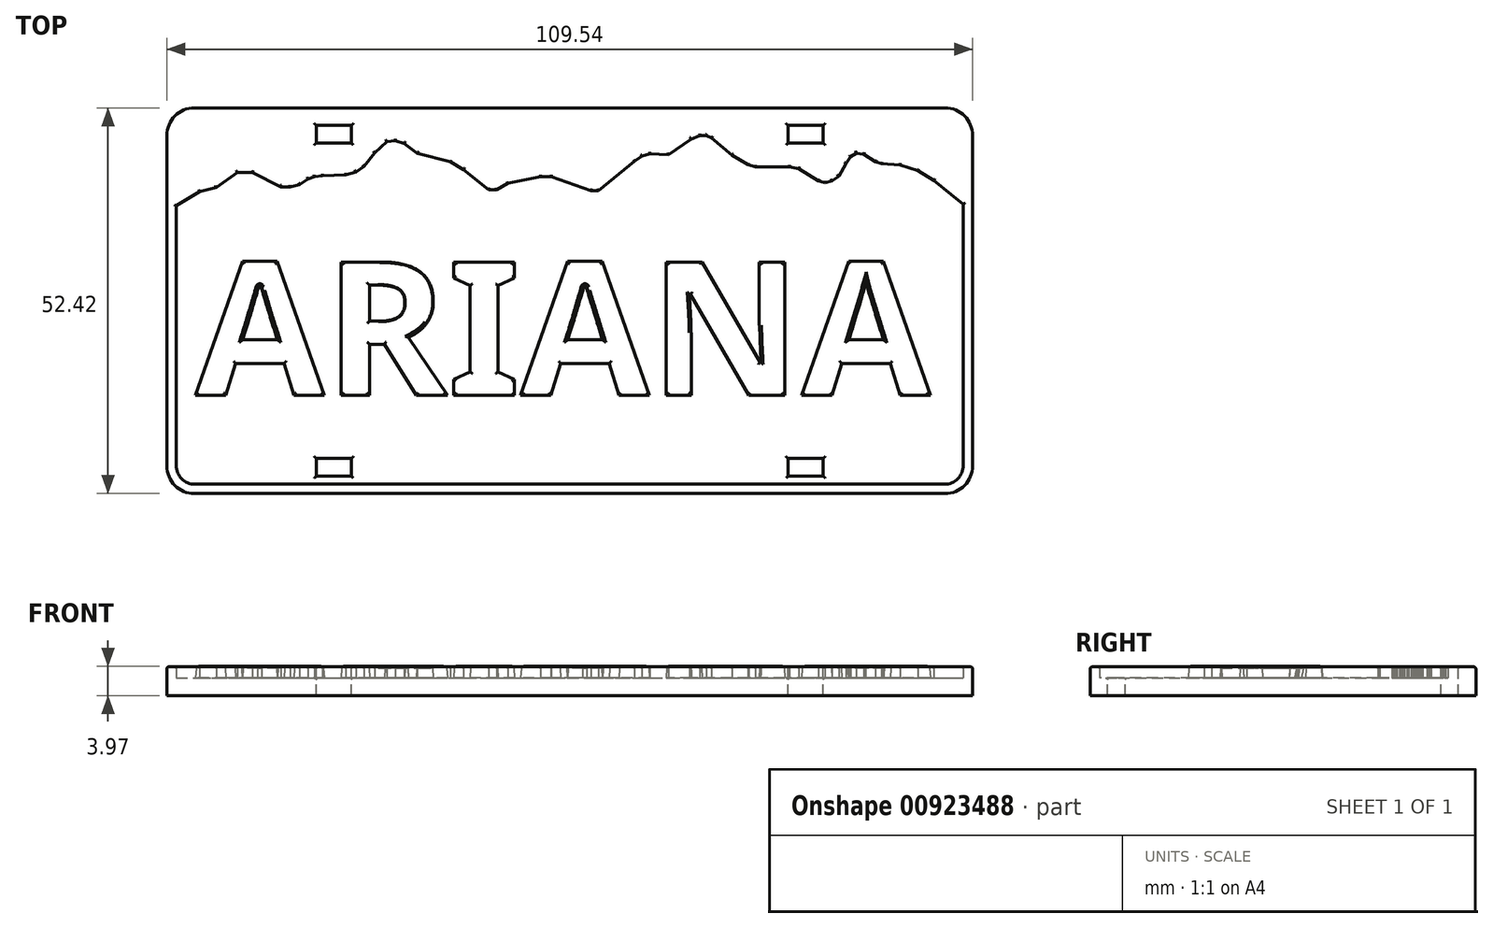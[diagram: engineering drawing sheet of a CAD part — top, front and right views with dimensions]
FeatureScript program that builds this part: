
annotation { "Feature Type Name" : "Feature", "Feature Type Description" : "" }
export const myFeature = defineFeature(function(context is Context, id is Id, definition is map)
    precondition{}
    {
        {
            var Q0;
            Q0=qCreatedBy(makeId("Top.planeOp"),FACE);
            var sketch = newSketch(context, id + "F0", { "sketchPlane" : qUnion([Q0])});
            skLineSegment(sketch, "E0", {"start": v(54.77, -22.46) * mm, "end": v(54.77, 22.46) * mm});
            skArc(sketch, "E1", {"start": v(54.77, 22.46) * mm, "mid": v(53.68, 25.11) * mm, "end": v(51.02, 26.21) * mm});
            skLineSegment(sketch, "E2", {"start": v(51.02, 26.21) * mm, "end": v(-51.02, 26.21) * mm});
            skArc(sketch, "E3", {"start": v(-51.02, 26.21) * mm, "mid": v(-53.68, 25.11) * mm, "end": v(-54.77, 22.46) * mm});
            skLineSegment(sketch, "E4", {"start": v(-54.77, 22.46) * mm, "end": v(-54.77, -22.46) * mm});
            skArc(sketch, "E5", {"start": v(-54.77, -22.46) * mm, "mid": v(-53.54, -25.24) * mm, "end": v(-50.64, -26.2) * mm});
            skLineSegment(sketch, "E6", {"start": v(-50.64, -26.2) * mm, "end": v(51.04, -26.2) * mm});
            skArc(sketch, "E7", {"start": v(51.02, -26.21) * mm, "mid": v(53.68, -25.11) * mm, "end": v(54.77, -22.46) * mm});
            skLineSegment(sketch, "E8", {"start": v(-54.77, 12.13) * mm, "end": v(-50.31, 14.84) * mm});
            skLineSegment(sketch, "E9", {"start": v(-50.31, 14.84) * mm, "end": v(-48.06, 15.4) * mm});
            skLineSegment(sketch, "E10", {"start": v(-48.06, 15.4) * mm, "end": v(-45.2, 17.44) * mm});
            skLineSegment(sketch, "E11", {"start": v(-45.2, 17.44) * mm, "end": v(-43.14, 17.44) * mm});
            skLineSegment(sketch, "E12", {"start": v(-43.14, 17.44) * mm, "end": v(-39.3, 15.5) * mm});
            skLineSegment(sketch, "E13", {"start": v(-39.3, 15.5) * mm, "end": v(-38.03, 15.49) * mm});
            skLineSegment(sketch, "E14", {"start": v(-38.03, 15.49) * mm, "end": v(-36.75, 15.8) * mm});
            skLineSegment(sketch, "E15", {"start": v(-36.75, 15.8) * mm, "end": v(-35.57, 16.54) * mm});
            skLineSegment(sketch, "E16", {"start": v(-35.57, 16.54) * mm, "end": v(-34.73, 16.88) * mm});
            skLineSegment(sketch, "E17", {"start": v(-34.73, 16.88) * mm, "end": v(-33.6, 17.01) * mm});
            skLineSegment(sketch, "E18", {"start": v(-33.6, 17.01) * mm, "end": v(-30.43, 17.11) * mm});
            skLineSegment(sketch, "E19", {"start": v(-29.05, 17.5) * mm, "end": v(-27.98, 18.27) * mm});
            skLineSegment(sketch, "E20", {"start": v(-27.98, 18.27) * mm, "end": v(-26.53, 20.14) * mm});
            skLineSegment(sketch, "E21", {"start": v(-26.53, 20.14) * mm, "end": v(-24.88, 21.63) * mm});
            skLineSegment(sketch, "E22", {"start": v(-24.88, 21.63) * mm, "end": v(-23.73, 21.77) * mm});
            skLineSegment(sketch, "E23", {"start": v(-22.5, 21.4) * mm, "end": v(-20.72, 20.04) * mm});
            skLineSegment(sketch, "E24", {"start": v(-16.23, 18.87) * mm, "end": v(-14.45, 17.85) * mm});
            skLineSegment(sketch, "E25", {"start": v(-14.45, 17.85) * mm, "end": v(-11.02, 15.1) * mm});
            skLineSegment(sketch, "E26", {"start": v(-11.02, 15.1) * mm, "end": v(-9.93, 15.1) * mm});
            skLineSegment(sketch, "E27", {"start": v(-9.93, 15.1) * mm, "end": v(-8.4, 15.96) * mm});
            skLineSegment(sketch, "E28", {"start": v(-8.4, 15.96) * mm, "end": v(-3.94, 16.85) * mm});
            skLineSegment(sketch, "E29", {"start": v(-3.94, 16.85) * mm, "end": v(-2.54, 16.85) * mm});
            skLineSegment(sketch, "E30", {"start": v(-2.54, 16.85) * mm, "end": v(2.9, 14.97) * mm});
            skLineSegment(sketch, "E31", {"start": v(2.9, 14.97) * mm, "end": v(3.92, 14.97) * mm});
            skLineSegment(sketch, "E32", {"start": v(3.92, 14.97) * mm, "end": v(8.8, 18.97) * mm});
            skLineSegment(sketch, "E33", {"start": v(8.8, 18.97) * mm, "end": v(9.82, 19.64) * mm});
            skLineSegment(sketch, "E34", {"start": v(9.82, 19.64) * mm, "end": v(10.9, 19.97) * mm});
            skLineSegment(sketch, "E35", {"start": v(10.9, 19.97) * mm, "end": v(13.43, 19.86) * mm});
            skLineSegment(sketch, "E36", {"start": v(16.5, 21.96) * mm, "end": v(17.71, 22.42) * mm});
            skLineSegment(sketch, "E37", {"start": v(17.71, 22.42) * mm, "end": v(18.56, 22.45) * mm});
            skLineSegment(sketch, "E38", {"start": v(18.56, 22.45) * mm, "end": v(19.28, 22.13) * mm});
            skLineSegment(sketch, "E39", {"start": v(19.28, 22.13) * mm, "end": v(22.05, 19.8) * mm});
            skLineSegment(sketch, "E40", {"start": v(22.05, 19.8) * mm, "end": v(24.2, 18.5) * mm});
            skLineSegment(sketch, "E41", {"start": v(24.2, 18.5) * mm, "end": v(25.23, 18.2) * mm});
            skLineSegment(sketch, "E42", {"start": v(25.23, 18.2) * mm, "end": v(29.85, 18.2) * mm});
            skLineSegment(sketch, "E43", {"start": v(29.85, 18.2) * mm, "end": v(31.13, 17.95) * mm});
            skLineSegment(sketch, "E44", {"start": v(31.13, 17.95) * mm, "end": v(33.84, 16.27) * mm});
            skLineSegment(sketch, "E45", {"start": v(33.84, 16.27) * mm, "end": v(34.73, 16.06) * mm});
            skLineSegment(sketch, "E46", {"start": v(34.73, 16.06) * mm, "end": v(35.67, 16.3) * mm});
            skLineSegment(sketch, "E47", {"start": v(35.67, 16.3) * mm, "end": v(36.58, 16.95) * mm});
            skLineSegment(sketch, "E48", {"start": v(36.58, 16.95) * mm, "end": v(37.58, 18.67) * mm});
            skLineSegment(sketch, "E49", {"start": v(38.22, 19.58) * mm, "end": v(38.96, 20.06) * mm});
            skLineSegment(sketch, "E50", {"start": v(38.96, 20.06) * mm, "end": v(39.94, 19.92) * mm});
            skLineSegment(sketch, "E51", {"start": v(41.58, 18.88) * mm, "end": v(42.4, 18.61) * mm});
            skLineSegment(sketch, "E52", {"start": v(42.4, 18.61) * mm, "end": v(44.9, 18.47) * mm});
            skLineSegment(sketch, "E53", {"start": v(44.9, 18.47) * mm, "end": v(47.31, 17.68) * mm});
            skLineSegment(sketch, "E54", {"start": v(47.31, 17.68) * mm, "end": v(49.47, 16.33) * mm});
            skLineSegment(sketch, "E55", {"start": v(49.47, 16.33) * mm, "end": v(51.88, 14.42) * mm});
            skLineSegment(sketch, "E56", {"start": v(51.88, 14.42) * mm, "end": v(53.78, 12.92) * mm});
            skLineSegment(sketch, "E57", {"start": v(53.78, 12.92) * mm, "end": v(54.77, 12.06) * mm});
            skLineSegment(sketch, "E58", {"start": v(-20.72, 20.04) * mm, "end": v(-16.23, 18.87) * mm});
            skLineSegment(sketch, "E59", {"start": v(16.5, 21.96) * mm, "end": v(13.43, 19.86) * mm});
            skLineSegment(sketch, "E60", {"start": v(-22.5, 21.4) * mm, "end": v(-23.73, 21.77) * mm});
            skLineSegment(sketch, "E61", {"start": v(-29.05, 17.5) * mm, "end": v(-30.43, 17.11) * mm});
            skLineSegment(sketch, "E62", {"start": v(37.58, 18.67) * mm, "end": v(38.22, 19.58) * mm});
            skLineSegment(sketch, "E63", {"start": v(41.58, 18.88) * mm, "end": v(39.94, 19.92) * mm});
            skSolve(sketch);
        }
        {
            var Q0;
            Q0=qCreatedBy(makeId("Top.planeOp"),FACE);
            var sketch = newSketch(context, id + "F1", { "sketchPlane" : qUnion([Q0])});
            skLineSegment(sketch, "E64", {"start": v(54.77, -22.46) * mm, "end": v(54.77, 22.46) * mm});
            skArc(sketch, "E65", {"start": v(54.77, 22.46) * mm, "mid": v(53.68, 25.11) * mm, "end": v(51.02, 26.21) * mm});
            skLineSegment(sketch, "E66", {"start": v(51.02, 26.21) * mm, "end": v(-51.02, 26.21) * mm});
            skArc(sketch, "E67", {"start": v(-51.02, 26.21) * mm, "mid": v(-53.68, 25.11) * mm, "end": v(-54.77, 22.46) * mm});
            skLineSegment(sketch, "E68", {"start": v(-54.77, 22.46) * mm, "end": v(-54.77, -22.46) * mm});
            skArc(sketch, "E69", {"start": v(-54.77, -22.46) * mm, "mid": v(-53.68, -25.11) * mm, "end": v(-51.02, -26.21) * mm});
            skLineSegment(sketch, "E70", {"start": v(-51.02, -26.21) * mm, "end": v(51.02, -26.21) * mm});
            skArc(sketch, "E71", {"start": v(51.02, -26.21) * mm, "mid": v(53.68, -25.11) * mm, "end": v(54.77, -22.46) * mm});
            skLineSegment(sketch, "E72.0", {"start": v(50.96, 24.94) * mm, "end": v(-50.96, 24.94) * mm, "construction": true});
            skLineSegment(sketch, "E72.1", {"start": v(53.5, -22.4) * mm, "end": v(53.5, 22.4) * mm, "construction": true});
            skLineSegment(sketch, "E72.2", {"start": v(-50.96, -24.94) * mm, "end": v(50.96, -24.94) * mm, "construction": true});
            skLineSegment(sketch, "E72.3", {"start": v(-53.5, 22.4) * mm, "end": v(-53.5, -22.4) * mm, "construction": true});
            skPoint(sketch, "E73.visualSharp", {"position": v(-53.5, 24.94) * mm});
            skArc(sketch, "E73.filletArc", {"start": v(-50.96, 24.94) * mm, "mid": v(-52.76, 24.2) * mm, "end": v(-53.5, 22.4) * mm, "construction": true});
            skPoint(sketch, "E74.visualSharp", {"position": v(-53.5, -24.94) * mm});
            skArc(sketch, "E74.filletArc", {"start": v(-53.5, -22.4) * mm, "mid": v(-52.76, -24.2) * mm, "end": v(-50.96, -24.94) * mm, "construction": true});
            skPoint(sketch, "E75.visualSharp", {"position": v(53.5, -24.94) * mm});
            skArc(sketch, "E75.filletArc", {"start": v(50.96, -24.94) * mm, "mid": v(52.76, -24.2) * mm, "end": v(53.5, -22.4) * mm, "construction": true});
            skPoint(sketch, "E76.visualSharp", {"position": v(53.5, 24.94) * mm});
            skArc(sketch, "E76.filletArc", {"start": v(53.5, 22.4) * mm, "mid": v(52.76, 24.2) * mm, "end": v(50.96, 24.94) * mm, "construction": true});
            skSolve(sketch);
        }
        {
            var Q0;
            {var subQ3=sQuery(id+"F0.wireOp",EDGE,"E1");Q0=makeQuery(id+"F0.imprint","IMPRINT",FACE,{"disambiguationData":[TD([[makeQuery(id+"F0.imprint","IMPRINT",EDGE,{"derivedFrom":subQ3}),1.0]])]});}
            extrude(context, id + "F2", {"entities" : qUnion([Q0]), "depth" : 1.52 * mm, "offsetDistance" : 25.4 * mm});
        }
        {
            var Q0;
            Q0=qSketchRegion(id+"F1",true);
            extrude(context, id + "F3", {"entities" : qUnion([Q0]), "operationType" : NewBodyOperationType.ADD, "oppositeDirection" : true, "depth" : 2.38 * mm, "offsetDistance" : 25.4 * mm});
        }
        {
            var Q0;
            {var subQ58=sQuery(id+"F0.wireOp",EDGE,"E0");var subQ59=sQuery(id+"F1.wireOp",EDGE,"E64");var subQ60=sQuery(id+"F1.wireOp",EDGE,"E65");var subQ61=sQuery(id+"F1.wireOp",EDGE,"E68");var subQ62=sQuery(id+"F1.wireOp",EDGE,"E69");var subQ63=sQuery(id+"F1.wireOp",EDGE,"E70");var subQ64=sQuery(id+"F1.wireOp",EDGE,"E71");Q0=makeQuery(id+"F3.boolean.opBoolean","SPLIT",FACE,{"disambiguationData":[TD([makeQuery(id+"F2.opExtrude","SWEPT_FACE",FACE,{"disambiguationData":[OSD([subQ58])]})])],"derivedFrom":makeQuery(id+"F3.opExtrude","CAP_FACE",FACE,{"disambiguationData":[OSD([subQ59,subQ60,sQuery(id+"F1.wireOp",EDGE,"E66"),sQuery(id+"F1.wireOp",EDGE,"E67"),subQ61,subQ62,subQ63,subQ64])],"isStart":true})});}
            var sketch = newSketch(context, id + "F4", { "sketchPlane" : qUnion([Q0])});
            skLineSegment(sketch, "E77", {"start": v(54.77, -22.46) * mm, "end": v(54.77, 12.06) * mm});
            skLineSegment(sketch, "E78", {"start": v(-54.77, 12.13) * mm, "end": v(-54.77, -22.46) * mm});
            skArc(sketch, "E79", {"start": v(-54.77, -22.46) * mm, "mid": v(-53.68, -25.11) * mm, "end": v(-51.02, -26.21) * mm});
            skLineSegment(sketch, "E80", {"start": v(-51.02, -26.21) * mm, "end": v(51.02, -26.21) * mm});
            skArc(sketch, "E81", {"start": v(51.02, -26.21) * mm, "mid": v(53.68, -25.11) * mm, "end": v(54.77, -22.46) * mm});
            skLineSegment(sketch, "E82.1", {"start": v(53.5, -22.4) * mm, "end": v(53.5, 13.14) * mm});
            skLineSegment(sketch, "E82.2", {"start": v(-50.96, -24.94) * mm, "end": v(50.96, -24.94) * mm});
            skLineSegment(sketch, "E82.3", {"start": v(-53.5, 12.9) * mm, "end": v(-53.5, -22.4) * mm});
            skPoint(sketch, "E83.visualSharp", {"position": v(-53.5, 24.94) * mm});
            skPoint(sketch, "E84.visualSharp", {"position": v(-53.5, -24.94) * mm});
            skArc(sketch, "E84.filletArc", {"start": v(-53.5, -22.4) * mm, "mid": v(-52.76, -24.2) * mm, "end": v(-50.96, -24.94) * mm});
            skPoint(sketch, "E85.visualSharp", {"position": v(53.5, -24.94) * mm});
            skArc(sketch, "E85.filletArc", {"start": v(50.96, -24.94) * mm, "mid": v(52.76, -24.2) * mm, "end": v(53.5, -22.4) * mm});
            skPoint(sketch, "E86.visualSharp", {"position": v(53.5, 24.94) * mm});
            skLineSegment(sketch, "E87", {"start": v(-54.77, 12.13) * mm, "end": v(-53.5, 12.9) * mm});
            skLineSegment(sketch, "E88", {"start": v(53.5, 13.14) * mm, "end": v(53.78, 12.92) * mm});
            skLineSegment(sketch, "E89", {"start": v(53.78, 12.92) * mm, "end": v(54.77, 12.06) * mm});
            skSolve(sketch);
        }
        {
            var Q0;
            Q0=qSketchRegion(id+"F4",true);
            extrude(context, id + "F5", {"entities" : qUnion([Q0]), "operationType" : NewBodyOperationType.ADD, "depth" : 1.52 * mm, "offsetDistance" : 25.4 * mm});
        }
        {
            var Q0;
            Q0=makeQuery(id+"F5.boolean.opBoolean","MERGE",FACE,{"derivedFrom":[makeQuery(id+"F2.opExtrude","CAP_FACE",FACE,{"disambiguationData":[OSD([sQuery(id+"F0.wireOp",EDGE,"E0"),sQuery(id+"F0.wireOp",EDGE,"E1"),sQuery(id+"F0.wireOp",EDGE,"E2"),sQuery(id+"F0.wireOp",EDGE,"E3"),sQuery(id+"F0.wireOp",EDGE,"E4"),sQuery(id+"F0.wireOp",EDGE,"E8"),sQuery(id+"F0.wireOp",EDGE,"E9"),sQuery(id+"F0.wireOp",EDGE,"E10"),sQuery(id+"F0.wireOp",EDGE,"E11"),sQuery(id+"F0.wireOp",EDGE,"E12"),sQuery(id+"F0.wireOp",EDGE,"E13"),sQuery(id+"F0.wireOp",EDGE,"E14"),sQuery(id+"F0.wireOp",EDGE,"E15"),sQuery(id+"F0.wireOp",EDGE,"E16"),sQuery(id+"F0.wireOp",EDGE,"E17"),sQuery(id+"F0.wireOp",EDGE,"E18"),sQuery(id+"F0.wireOp",EDGE,"7b9f405e-0691-426e-9c9e-a5372cf0836a"),sQuery(id+"F0.wireOp",EDGE,"E19"),sQuery(id+"F0.wireOp",EDGE,"E20"),sQuery(id+"F0.wireOp",EDGE,"E21"),sQuery(id+"F0.wireOp",EDGE,"E22"),sQuery(id+"F0.wireOp",EDGE,"b3dec5b1-662c-4d50-a13c-af7b7760114a"),sQuery(id+"F0.wireOp",EDGE,"E23"),sQuery(id+"F0.wireOp",EDGE,"4d9ee76e-0833-4cdc-b1a8-2d4ce76e6521"),sQuery(id+"F0.wireOp",EDGE,"E24"),sQuery(id+"F0.wireOp",EDGE,"E25"),sQuery(id+"F0.wireOp",EDGE,"E26"),sQuery(id+"F0.wireOp",EDGE,"E27"),sQuery(id+"F0.wireOp",EDGE,"E28"),sQuery(id+"F0.wireOp",EDGE,"E29"),sQuery(id+"F0.wireOp",EDGE,"E30"),sQuery(id+"F0.wireOp",EDGE,"E31"),sQuery(id+"F0.wireOp",EDGE,"E32"),sQuery(id+"F0.wireOp",EDGE,"E33"),sQuery(id+"F0.wireOp",EDGE,"E34"),sQuery(id+"F0.wireOp",EDGE,"E35"),sQuery(id+"F0.wireOp",EDGE,"55551997-bb9e-4b94-90c5-def3cb147476"),sQuery(id+"F0.wireOp",EDGE,"E36"),sQuery(id+"F0.wireOp",EDGE,"E37"),sQuery(id+"F0.wireOp",EDGE,"E38"),sQuery(id+"F0.wireOp",EDGE,"E39"),sQuery(id+"F0.wireOp",EDGE,"E40"),sQuery(id+"F0.wireOp",EDGE,"E41"),sQuery(id+"F0.wireOp",EDGE,"E42"),sQuery(id+"F0.wireOp",EDGE,"E43"),sQuery(id+"F0.wireOp",EDGE,"E44"),sQuery(id+"F0.wireOp",EDGE,"E45"),sQuery(id+"F0.wireOp",EDGE,"E46"),sQuery(id+"F0.wireOp",EDGE,"E47"),sQuery(id+"F0.wireOp",EDGE,"E48"),sQuery(id+"F0.wireOp",EDGE,"513b7cbe-d979-4e22-b277-f3c42ccdbda1"),sQuery(id+"F0.wireOp",EDGE,"E49"),sQuery(id+"F0.wireOp",EDGE,"E50"),sQuery(id+"F0.wireOp",EDGE,"0d842e13-672c-40e3-aae4-28923e78d4e0"),sQuery(id+"F0.wireOp",EDGE,"E51"),sQuery(id+"F0.wireOp",EDGE,"E52"),sQuery(id+"F0.wireOp",EDGE,"E53"),sQuery(id+"F0.wireOp",EDGE,"E54"),sQuery(id+"F0.wireOp",EDGE,"E55"),sQuery(id+"F0.wireOp",EDGE,"E56"),sQuery(id+"F0.wireOp",EDGE,"E57")])],"isStart":false}),makeQuery(id+"F5.opExtrude","CAP_FACE",FACE,{"disambiguationData":[OSD([sQuery(id+"F4.wireOp",EDGE,"E77"),sQuery(id+"F4.wireOp",EDGE,"E78"),sQuery(id+"F4.wireOp",EDGE,"E79"),sQuery(id+"F4.wireOp",EDGE,"E80"),sQuery(id+"F4.wireOp",EDGE,"E81"),sQuery(id+"F4.wireOp",EDGE,"E82.1"),sQuery(id+"F4.wireOp",EDGE,"E82.2"),sQuery(id+"F4.wireOp",EDGE,"E82.3"),sQuery(id+"F4.wireOp",EDGE,"E84.filletArc"),sQuery(id+"F4.wireOp",EDGE,"E85.filletArc"),sQuery(id+"F4.wireOp",EDGE,"E87"),sQuery(id+"F4.wireOp",EDGE,"E88"),sQuery(id+"F4.wireOp",EDGE,"E89")])],"isStart":false})]});
            var sketch = newSketch(context, id + "F6", { "sketchPlane" : qUnion([Q0])});
            skLineSegment(sketch, "E90.bottom", {"start": v(-34.45, 23.83) * mm, "end": v(-29.7, 23.83) * mm});
            skLineSegment(sketch, "E90.top", {"start": v(-34.45, 21.45) * mm, "end": v(-29.7, 21.45) * mm});
            skLineSegment(sketch, "E90.left", {"start": v(-34.45, 23.83) * mm, "end": v(-34.45, 21.45) * mm});
            skLineSegment(sketch, "E90.right", {"start": v(-29.7, 23.83) * mm, "end": v(-29.7, 21.45) * mm});
            skLineSegment(sketch, "E91", {"start": v(0, 26.21) * mm, "end": v(0, -26.21) * mm, "construction": true});
            skLineSegment(sketch, "E92.MirrorCS", {"start": v(34.45, 23.83) * mm, "end": v(34.45, 21.45) * mm});
            skLineSegment(sketch, "E93.MirrorCS", {"start": v(29.7, 23.83) * mm, "end": v(29.7, 21.45) * mm});
            skLineSegment(sketch, "E94.MirrorCS", {"start": v(34.45, 21.45) * mm, "end": v(29.7, 21.45) * mm});
            skLineSegment(sketch, "E95.MirrorCS", {"start": v(34.45, 23.83) * mm, "end": v(29.7, 23.83) * mm});
            skLineSegment(sketch, "E96", {"start": v(0, 0) * mm, "end": v(-59.23, 0) * mm, "construction": true});
            skLineSegment(sketch, "E97", {"start": v(0, 0) * mm, "end": v(56.47, 0) * mm, "construction": true});
            skLineSegment(sketch, "E98.MirrorCS", {"start": v(-34.45, -23.83) * mm, "end": v(-29.7, -23.83) * mm});
            skLineSegment(sketch, "E99.MirrorCS", {"start": v(-34.45, -23.83) * mm, "end": v(-34.45, -21.45) * mm});
            skLineSegment(sketch, "E100.MirrorCS", {"start": v(-34.45, -21.45) * mm, "end": v(-29.7, -21.45) * mm});
            skLineSegment(sketch, "E101.MirrorCS", {"start": v(-29.7, -23.83) * mm, "end": v(-29.7, -21.45) * mm});
            skLineSegment(sketch, "E102.MirrorCS", {"start": v(29.7, -23.83) * mm, "end": v(29.7, -21.45) * mm});
            skLineSegment(sketch, "E103.MirrorCS", {"start": v(34.45, -23.83) * mm, "end": v(29.7, -23.83) * mm});
            skLineSegment(sketch, "E104.MirrorCS", {"start": v(34.45, -23.83) * mm, "end": v(34.45, -21.45) * mm});
            skLineSegment(sketch, "E105.MirrorCS", {"start": v(34.45, -21.45) * mm, "end": v(29.7, -21.45) * mm});
            skSolve(sketch);
        }
        {
            var Q0;
            Q0=qSketchRegion(id+"F6",true);
            extrude(context, id + "F7", {"entities" : qUnion([Q0]), "operationType" : NewBodyOperationType.REMOVE, "endBound" : BoundingType.THROUGH_ALL, "oppositeDirection" : true, "depth" : 25.4 * mm, "offsetDistance" : 25.4 * mm});
        }
        {
            var Q0;
            Q0=makeQuery(id+"F3.opExtrude","CAP_FACE",FACE,{"disambiguationData":[OSD([sQuery(id+"F1.wireOp",EDGE,"E64"),sQuery(id+"F1.wireOp",EDGE,"E65"),sQuery(id+"F1.wireOp",EDGE,"E66"),sQuery(id+"F1.wireOp",EDGE,"E67"),sQuery(id+"F1.wireOp",EDGE,"E68"),sQuery(id+"F1.wireOp",EDGE,"E69"),sQuery(id+"F1.wireOp",EDGE,"E70"),sQuery(id+"F1.wireOp",EDGE,"E71")])],"isStart":true});
            var sketch = newSketch(context, id + "F8", { "sketchPlane" : qUnion([Q0])});
            skText(sketch, "E106", { "text": "ARIANA", "fontName": "NotoSans-Bold.ttf"});
            const initialGuessF8  = {"E106": [-0.0509, -0.01287, 1, 0, 0.0183]};
            skSetInitialGuess(sketch, initialGuessF8);
            skSolve(sketch);
        }
        {
            var Q0;
            Q0=qSketchRegion(id+"F8",true);
            extrude(context, id + "F9", {"entities" : qUnion([Q0]), "operationType" : NewBodyOperationType.ADD, "depth" : 1.59 * mm, "offsetDistance" : 25.4 * mm, "hasDraft" : true, "draftAngle" : 3 * degree, "draftPullDirection" : true});
        }
        {
            var Q0;
            Q0=makeQuery(id+"F5.boolean.opBoolean","MERGE",FACE,{"derivedFrom":[makeQuery(id+"F2.opExtrude","CAP_FACE",FACE,{"disambiguationData":[OSD([sQuery(id+"F0.wireOp",EDGE,"E0"),sQuery(id+"F0.wireOp",EDGE,"E1"),sQuery(id+"F0.wireOp",EDGE,"E2"),sQuery(id+"F0.wireOp",EDGE,"E3"),sQuery(id+"F0.wireOp",EDGE,"E4"),sQuery(id+"F0.wireOp",EDGE,"E8"),sQuery(id+"F0.wireOp",EDGE,"E9"),sQuery(id+"F0.wireOp",EDGE,"E10"),sQuery(id+"F0.wireOp",EDGE,"E11"),sQuery(id+"F0.wireOp",EDGE,"E12"),sQuery(id+"F0.wireOp",EDGE,"E13"),sQuery(id+"F0.wireOp",EDGE,"E14"),sQuery(id+"F0.wireOp",EDGE,"E15"),sQuery(id+"F0.wireOp",EDGE,"E16"),sQuery(id+"F0.wireOp",EDGE,"E17"),sQuery(id+"F0.wireOp",EDGE,"E18"),sQuery(id+"F0.wireOp",EDGE,"E19"),sQuery(id+"F0.wireOp",EDGE,"E20"),sQuery(id+"F0.wireOp",EDGE,"E21"),sQuery(id+"F0.wireOp",EDGE,"E22"),sQuery(id+"F0.wireOp",EDGE,"E23"),sQuery(id+"F0.wireOp",EDGE,"E24"),sQuery(id+"F0.wireOp",EDGE,"E25"),sQuery(id+"F0.wireOp",EDGE,"E26"),sQuery(id+"F0.wireOp",EDGE,"E27"),sQuery(id+"F0.wireOp",EDGE,"E28"),sQuery(id+"F0.wireOp",EDGE,"E29"),sQuery(id+"F0.wireOp",EDGE,"E30"),sQuery(id+"F0.wireOp",EDGE,"E31"),sQuery(id+"F0.wireOp",EDGE,"E32"),sQuery(id+"F0.wireOp",EDGE,"E33"),sQuery(id+"F0.wireOp",EDGE,"E34"),sQuery(id+"F0.wireOp",EDGE,"E35"),sQuery(id+"F0.wireOp",EDGE,"E36"),sQuery(id+"F0.wireOp",EDGE,"E37"),sQuery(id+"F0.wireOp",EDGE,"E38"),sQuery(id+"F0.wireOp",EDGE,"E39"),sQuery(id+"F0.wireOp",EDGE,"E40"),sQuery(id+"F0.wireOp",EDGE,"E41"),sQuery(id+"F0.wireOp",EDGE,"E42"),sQuery(id+"F0.wireOp",EDGE,"E43"),sQuery(id+"F0.wireOp",EDGE,"E44"),sQuery(id+"F0.wireOp",EDGE,"E45"),sQuery(id+"F0.wireOp",EDGE,"E46"),sQuery(id+"F0.wireOp",EDGE,"E47"),sQuery(id+"F0.wireOp",EDGE,"E48"),sQuery(id+"F0.wireOp",EDGE,"E49"),sQuery(id+"F0.wireOp",EDGE,"E50"),sQuery(id+"F0.wireOp",EDGE,"E51"),sQuery(id+"F0.wireOp",EDGE,"E52"),sQuery(id+"F0.wireOp",EDGE,"E53"),sQuery(id+"F0.wireOp",EDGE,"E54"),sQuery(id+"F0.wireOp",EDGE,"E55"),sQuery(id+"F0.wireOp",EDGE,"E56"),sQuery(id+"F0.wireOp",EDGE,"E57"),sQuery(id+"F0.wireOp",EDGE,"E58"),sQuery(id+"F0.wireOp",EDGE,"E59"),sQuery(id+"F0.wireOp",EDGE,"E60"),sQuery(id+"F0.wireOp",EDGE,"E61"),sQuery(id+"F0.wireOp",EDGE,"E62"),sQuery(id+"F0.wireOp",EDGE,"E63")])],"isStart":false}),makeQuery(id+"F5.opExtrude","CAP_FACE",FACE,{"disambiguationData":[OSD([sQuery(id+"F4.wireOp",EDGE,"E77"),sQuery(id+"F4.wireOp",EDGE,"E78"),sQuery(id+"F4.wireOp",EDGE,"E79"),sQuery(id+"F4.wireOp",EDGE,"E80"),sQuery(id+"F4.wireOp",EDGE,"E81"),sQuery(id+"F4.wireOp",EDGE,"E82.1"),sQuery(id+"F4.wireOp",EDGE,"E82.2"),sQuery(id+"F4.wireOp",EDGE,"E82.3"),sQuery(id+"F4.wireOp",EDGE,"E84.filletArc"),sQuery(id+"F4.wireOp",EDGE,"E85.filletArc"),sQuery(id+"F4.wireOp",EDGE,"E87"),sQuery(id+"F4.wireOp",EDGE,"E88"),sQuery(id+"F4.wireOp",EDGE,"E89")])],"isStart":false})]});
            var Q1;
            Q1=makeQuery(id+"F9.opExtrude","CAP_FACE",FACE,{"disambiguationData":[OSD([sQuery(id+"F8.wireOp",EDGE,"E106.sketch_text.stroke-0"),sQuery(id+"F8.wireOp",EDGE,"E106.sketch_text.stroke-1"),sQuery(id+"F8.wireOp",EDGE,"E106.sketch_text.stroke-2"),sQuery(id+"F8.wireOp",EDGE,"E106.sketch_text.stroke-3"),sQuery(id+"F8.wireOp",EDGE,"E106.sketch_text.stroke-4"),sQuery(id+"F8.wireOp",EDGE,"E106.sketch_text.stroke-5"),sQuery(id+"F8.wireOp",EDGE,"E106.sketch_text.stroke-6"),sQuery(id+"F8.wireOp",EDGE,"E106.sketch_text.stroke-7"),sQuery(id+"F8.wireOp",EDGE,"E106.sketch_text.stroke-8"),sQuery(id+"F8.wireOp",EDGE,"E106.sketch_text.stroke-9"),sQuery(id+"F8.wireOp",EDGE,"E106.sketch_text.stroke-10"),sQuery(id+"F8.wireOp",EDGE,"E106.sketch_text.stroke-11")])],"isStart":false});
            var Q2;
            Q2=makeQuery(id+"F9.opExtrude","CAP_FACE",FACE,{"disambiguationData":[OSD([sQuery(id+"F8.wireOp",EDGE,"E106.sketch_text.stroke-12"),sQuery(id+"F8.wireOp",EDGE,"E106.sketch_text.stroke-13"),sQuery(id+"F8.wireOp",EDGE,"E106.sketch_text.stroke-14"),sQuery(id+"F8.wireOp",EDGE,"E106.sketch_text.stroke-15"),sQuery(id+"F8.wireOp",EDGE,"E106.sketch_text.stroke-16"),sQuery(id+"F8.wireOp",EDGE,"E106.sketch_text.stroke-17"),sQuery(id+"F8.wireOp",EDGE,"E106.sketch_text.stroke-18"),sQuery(id+"F8.wireOp",EDGE,"E106.sketch_text.stroke-19"),sQuery(id+"F8.wireOp",EDGE,"E106.sketch_text.stroke-20"),sQuery(id+"F8.wireOp",EDGE,"E106.sketch_text.stroke-21"),sQuery(id+"F8.wireOp",EDGE,"E106.sketch_text.stroke-22"),sQuery(id+"F8.wireOp",EDGE,"E106.sketch_text.stroke-23"),sQuery(id+"F8.wireOp",EDGE,"E106.sketch_text.stroke-24"),sQuery(id+"F8.wireOp",EDGE,"E106.sketch_text.stroke-25"),sQuery(id+"F8.wireOp",EDGE,"E106.sketch_text.stroke-26"),sQuery(id+"F8.wireOp",EDGE,"E106.sketch_text.stroke-27"),sQuery(id+"F8.wireOp",EDGE,"E106.sketch_text.stroke-28"),sQuery(id+"F8.wireOp",EDGE,"E106.sketch_text.stroke-29"),sQuery(id+"F8.wireOp",EDGE,"E106.sketch_text.stroke-30")])],"isStart":false});
            var Q3;
            Q3=makeQuery(id+"F9.opExtrude","CAP_FACE",FACE,{"disambiguationData":[OSD([sQuery(id+"F8.wireOp",EDGE,"E106.sketch_text.stroke-31"),sQuery(id+"F8.wireOp",EDGE,"E106.sketch_text.stroke-32"),sQuery(id+"F8.wireOp",EDGE,"E106.sketch_text.stroke-33"),sQuery(id+"F8.wireOp",EDGE,"E106.sketch_text.stroke-34"),sQuery(id+"F8.wireOp",EDGE,"E106.sketch_text.stroke-35"),sQuery(id+"F8.wireOp",EDGE,"E106.sketch_text.stroke-36"),sQuery(id+"F8.wireOp",EDGE,"E106.sketch_text.stroke-37"),sQuery(id+"F8.wireOp",EDGE,"E106.sketch_text.stroke-38"),sQuery(id+"F8.wireOp",EDGE,"E106.sketch_text.stroke-39"),sQuery(id+"F8.wireOp",EDGE,"E106.sketch_text.stroke-40"),sQuery(id+"F8.wireOp",EDGE,"E106.sketch_text.stroke-41"),sQuery(id+"F8.wireOp",EDGE,"E106.sketch_text.stroke-42")])],"isStart":false});
            var Q4;
            Q4=makeQuery(id+"F9.opExtrude","CAP_FACE",FACE,{"disambiguationData":[OSD([sQuery(id+"F8.wireOp",EDGE,"E106.sketch_text.stroke-43"),sQuery(id+"F8.wireOp",EDGE,"E106.sketch_text.stroke-44"),sQuery(id+"F8.wireOp",EDGE,"E106.sketch_text.stroke-45"),sQuery(id+"F8.wireOp",EDGE,"E106.sketch_text.stroke-46"),sQuery(id+"F8.wireOp",EDGE,"E106.sketch_text.stroke-47"),sQuery(id+"F8.wireOp",EDGE,"E106.sketch_text.stroke-48"),sQuery(id+"F8.wireOp",EDGE,"E106.sketch_text.stroke-49"),sQuery(id+"F8.wireOp",EDGE,"E106.sketch_text.stroke-50"),sQuery(id+"F8.wireOp",EDGE,"E106.sketch_text.stroke-51"),sQuery(id+"F8.wireOp",EDGE,"E106.sketch_text.stroke-52"),sQuery(id+"F8.wireOp",EDGE,"E106.sketch_text.stroke-53"),sQuery(id+"F8.wireOp",EDGE,"E106.sketch_text.stroke-54")])],"isStart":false});
            var Q5;
            Q5=makeQuery(id+"F9.opExtrude","CAP_FACE",FACE,{"disambiguationData":[OSD([sQuery(id+"F8.wireOp",EDGE,"E106.sketch_text.stroke-55"),sQuery(id+"F8.wireOp",EDGE,"E106.sketch_text.stroke-56"),sQuery(id+"F8.wireOp",EDGE,"E106.sketch_text.stroke-57"),sQuery(id+"F8.wireOp",EDGE,"E106.sketch_text.stroke-58"),sQuery(id+"F8.wireOp",EDGE,"E106.sketch_text.stroke-59"),sQuery(id+"F8.wireOp",EDGE,"E106.sketch_text.stroke-60"),sQuery(id+"F8.wireOp",EDGE,"E106.sketch_text.stroke-61"),sQuery(id+"F8.wireOp",EDGE,"E106.sketch_text.stroke-62"),sQuery(id+"F8.wireOp",EDGE,"E106.sketch_text.stroke-63"),sQuery(id+"F8.wireOp",EDGE,"E106.sketch_text.stroke-64"),sQuery(id+"F8.wireOp",EDGE,"E106.sketch_text.stroke-65"),sQuery(id+"F8.wireOp",EDGE,"E106.sketch_text.stroke-66"),sQuery(id+"F8.wireOp",EDGE,"E106.sketch_text.stroke-67"),sQuery(id+"F8.wireOp",EDGE,"E106.sketch_text.stroke-68")])],"isStart":false});
            var Q6;
            Q6=makeQuery(id+"F9.opExtrude","CAP_FACE",FACE,{"disambiguationData":[OSD([sQuery(id+"F8.wireOp",EDGE,"E106.sketch_text.stroke-69"),sQuery(id+"F8.wireOp",EDGE,"E106.sketch_text.stroke-70"),sQuery(id+"F8.wireOp",EDGE,"E106.sketch_text.stroke-71"),sQuery(id+"F8.wireOp",EDGE,"E106.sketch_text.stroke-72"),sQuery(id+"F8.wireOp",EDGE,"E106.sketch_text.stroke-73"),sQuery(id+"F8.wireOp",EDGE,"E106.sketch_text.stroke-74"),sQuery(id+"F8.wireOp",EDGE,"E106.sketch_text.stroke-75"),sQuery(id+"F8.wireOp",EDGE,"E106.sketch_text.stroke-76"),sQuery(id+"F8.wireOp",EDGE,"E106.sketch_text.stroke-77"),sQuery(id+"F8.wireOp",EDGE,"E106.sketch_text.stroke-78"),sQuery(id+"F8.wireOp",EDGE,"E106.sketch_text.stroke-79"),sQuery(id+"F8.wireOp",EDGE,"E106.sketch_text.stroke-80"),sQuery(id+"F8.wireOp",EDGE,"E106.sketch_text.stroke-81"),sQuery(id+"F8.wireOp",EDGE,"E106.sketch_text.stroke-82")])],"isStart":false});
            var Q7;
            Q7=makeQuery(id+"F9.opExtrude","CAP_FACE",FACE,{"disambiguationData":[OSD([sQuery(id+"F8.wireOp",EDGE,"E106.sketch_text.stroke-83"),sQuery(id+"F8.wireOp",EDGE,"E106.sketch_text.stroke-84"),sQuery(id+"F8.wireOp",EDGE,"E106.sketch_text.stroke-85"),sQuery(id+"F8.wireOp",EDGE,"E106.sketch_text.stroke-86"),sQuery(id+"F8.wireOp",EDGE,"E106.sketch_text.stroke-87"),sQuery(id+"F8.wireOp",EDGE,"E106.sketch_text.stroke-88"),sQuery(id+"F8.wireOp",EDGE,"E106.sketch_text.stroke-89"),sQuery(id+"F8.wireOp",EDGE,"E106.sketch_text.stroke-90"),sQuery(id+"F8.wireOp",EDGE,"E106.sketch_text.stroke-91"),sQuery(id+"F8.wireOp",EDGE,"E106.sketch_text.stroke-92"),sQuery(id+"F8.wireOp",EDGE,"E106.sketch_text.stroke-93"),sQuery(id+"F8.wireOp",EDGE,"E106.sketch_text.stroke-94")])],"isStart":false});
            var Q8;
            Q8=makeQuery(id+"F7.boolean.opBoolean","INTERSECT",EDGE,{"derivedFrom":[makeQuery(id+"F3.opExtrude","CAP_FACE",FACE,{"disambiguationData":[OSD([sQuery(id+"F1.wireOp",EDGE,"E64"),sQuery(id+"F1.wireOp",EDGE,"E65"),sQuery(id+"F1.wireOp",EDGE,"E66"),sQuery(id+"F1.wireOp",EDGE,"E67"),sQuery(id+"F1.wireOp",EDGE,"E68"),sQuery(id+"F1.wireOp",EDGE,"E69"),sQuery(id+"F1.wireOp",EDGE,"E70"),sQuery(id+"F1.wireOp",EDGE,"E71")])],"isStart":true}),makeQuery(id+"F7.opExtrude","SWEPT_FACE",FACE,{"disambiguationData":[OSD([sQuery(id+"F6.wireOp",EDGE,"E99.MirrorCS")])]})]});
            var Q9;
            Q9=makeQuery(id+"F7.boolean.opBoolean","INTERSECT",EDGE,{"derivedFrom":[makeQuery(id+"F3.opExtrude","CAP_FACE",FACE,{"disambiguationData":[OSD([sQuery(id+"F1.wireOp",EDGE,"E64"),sQuery(id+"F1.wireOp",EDGE,"E65"),sQuery(id+"F1.wireOp",EDGE,"E66"),sQuery(id+"F1.wireOp",EDGE,"E67"),sQuery(id+"F1.wireOp",EDGE,"E68"),sQuery(id+"F1.wireOp",EDGE,"E69"),sQuery(id+"F1.wireOp",EDGE,"E70"),sQuery(id+"F1.wireOp",EDGE,"E71")])],"isStart":true}),makeQuery(id+"F7.opExtrude","SWEPT_FACE",FACE,{"disambiguationData":[OSD([sQuery(id+"F6.wireOp",EDGE,"E100.MirrorCS")])]})]});
            var Q10;
            Q10=makeQuery(id+"F7.boolean.opBoolean","INTERSECT",EDGE,{"derivedFrom":[makeQuery(id+"F3.opExtrude","CAP_FACE",FACE,{"disambiguationData":[OSD([sQuery(id+"F1.wireOp",EDGE,"E64"),sQuery(id+"F1.wireOp",EDGE,"E65"),sQuery(id+"F1.wireOp",EDGE,"E66"),sQuery(id+"F1.wireOp",EDGE,"E67"),sQuery(id+"F1.wireOp",EDGE,"E68"),sQuery(id+"F1.wireOp",EDGE,"E69"),sQuery(id+"F1.wireOp",EDGE,"E70"),sQuery(id+"F1.wireOp",EDGE,"E71")])],"isStart":true}),makeQuery(id+"F7.opExtrude","SWEPT_FACE",FACE,{"disambiguationData":[OSD([sQuery(id+"F6.wireOp",EDGE,"E98.MirrorCS")])]})]});
            var Q11;
            Q11=makeQuery(id+"F7.boolean.opBoolean","INTERSECT",EDGE,{"derivedFrom":[makeQuery(id+"F3.opExtrude","CAP_FACE",FACE,{"disambiguationData":[OSD([sQuery(id+"F1.wireOp",EDGE,"E64"),sQuery(id+"F1.wireOp",EDGE,"E65"),sQuery(id+"F1.wireOp",EDGE,"E66"),sQuery(id+"F1.wireOp",EDGE,"E67"),sQuery(id+"F1.wireOp",EDGE,"E68"),sQuery(id+"F1.wireOp",EDGE,"E69"),sQuery(id+"F1.wireOp",EDGE,"E70"),sQuery(id+"F1.wireOp",EDGE,"E71")])],"isStart":true}),makeQuery(id+"F7.opExtrude","SWEPT_FACE",FACE,{"disambiguationData":[OSD([sQuery(id+"F6.wireOp",EDGE,"E101.MirrorCS")])]})]});
            var Q12;
            Q12=makeQuery(id+"F7.boolean.opBoolean","INTERSECT",EDGE,{"derivedFrom":[makeQuery(id+"F3.opExtrude","CAP_FACE",FACE,{"disambiguationData":[OSD([sQuery(id+"F1.wireOp",EDGE,"E64"),sQuery(id+"F1.wireOp",EDGE,"E65"),sQuery(id+"F1.wireOp",EDGE,"E66"),sQuery(id+"F1.wireOp",EDGE,"E67"),sQuery(id+"F1.wireOp",EDGE,"E68"),sQuery(id+"F1.wireOp",EDGE,"E69"),sQuery(id+"F1.wireOp",EDGE,"E70"),sQuery(id+"F1.wireOp",EDGE,"E71")])],"isStart":true}),makeQuery(id+"F7.opExtrude","SWEPT_FACE",FACE,{"disambiguationData":[OSD([sQuery(id+"F6.wireOp",EDGE,"E105.MirrorCS")])]})]});
            var Q13;
            Q13=makeQuery(id+"F7.boolean.opBoolean","INTERSECT",EDGE,{"derivedFrom":[makeQuery(id+"F3.opExtrude","CAP_FACE",FACE,{"disambiguationData":[OSD([sQuery(id+"F1.wireOp",EDGE,"E64"),sQuery(id+"F1.wireOp",EDGE,"E65"),sQuery(id+"F1.wireOp",EDGE,"E66"),sQuery(id+"F1.wireOp",EDGE,"E67"),sQuery(id+"F1.wireOp",EDGE,"E68"),sQuery(id+"F1.wireOp",EDGE,"E69"),sQuery(id+"F1.wireOp",EDGE,"E70"),sQuery(id+"F1.wireOp",EDGE,"E71")])],"isStart":true}),makeQuery(id+"F7.opExtrude","SWEPT_FACE",FACE,{"disambiguationData":[OSD([sQuery(id+"F6.wireOp",EDGE,"E102.MirrorCS")])]})]});
            var Q14;
            Q14=makeQuery(id+"F7.boolean.opBoolean","INTERSECT",EDGE,{"derivedFrom":[makeQuery(id+"F3.opExtrude","CAP_FACE",FACE,{"disambiguationData":[OSD([sQuery(id+"F1.wireOp",EDGE,"E64"),sQuery(id+"F1.wireOp",EDGE,"E65"),sQuery(id+"F1.wireOp",EDGE,"E66"),sQuery(id+"F1.wireOp",EDGE,"E67"),sQuery(id+"F1.wireOp",EDGE,"E68"),sQuery(id+"F1.wireOp",EDGE,"E69"),sQuery(id+"F1.wireOp",EDGE,"E70"),sQuery(id+"F1.wireOp",EDGE,"E71")])],"isStart":true}),makeQuery(id+"F7.opExtrude","SWEPT_FACE",FACE,{"disambiguationData":[OSD([sQuery(id+"F6.wireOp",EDGE,"E103.MirrorCS")])]})]});
            var Q15;
            Q15=makeQuery(id+"F7.boolean.opBoolean","INTERSECT",EDGE,{"derivedFrom":[makeQuery(id+"F3.opExtrude","CAP_FACE",FACE,{"disambiguationData":[OSD([sQuery(id+"F1.wireOp",EDGE,"E64"),sQuery(id+"F1.wireOp",EDGE,"E65"),sQuery(id+"F1.wireOp",EDGE,"E66"),sQuery(id+"F1.wireOp",EDGE,"E67"),sQuery(id+"F1.wireOp",EDGE,"E68"),sQuery(id+"F1.wireOp",EDGE,"E69"),sQuery(id+"F1.wireOp",EDGE,"E70"),sQuery(id+"F1.wireOp",EDGE,"E71")])],"isStart":true}),makeQuery(id+"F7.opExtrude","SWEPT_FACE",FACE,{"disambiguationData":[OSD([sQuery(id+"F6.wireOp",EDGE,"E104.MirrorCS")])]})]});
            var Q16;
            Q16=makeQuery(id+"F9.opExtrude","SWEPT_EDGE",EDGE,{"disambiguationData":[OSD([sQuery(id+"F8.wireOp",EDGE,"E106.sketch_text.stroke-9"),sQuery(id+"F8.wireOp",EDGE,"E106.sketch_text.stroke-10")])]});
            var Q17;
            Q17=makeQuery(id+"F9.opExtrude","SWEPT_EDGE",EDGE,{"disambiguationData":[OSD([sQuery(id+"F8.wireOp",EDGE,"E106.sketch_text.stroke-52"),sQuery(id+"F8.wireOp",EDGE,"E106.sketch_text.stroke-53")])]});
            var Q18;
            Q18=makeQuery(id+"F9.opExtrude","SWEPT_EDGE",EDGE,{"disambiguationData":[OSD([sQuery(id+"F8.wireOp",EDGE,"E106.sketch_text.stroke-92"),sQuery(id+"F8.wireOp",EDGE,"E106.sketch_text.stroke-93")])]});
            fillet(context, id + "F10", {"entities" : qUnion([Q0, Q1, Q2, Q3, Q4, Q5, Q6, Q7, Q8, Q9, Q10, Q11, Q12, Q13, Q14, Q15, Q16, Q17, Q18]), "radius" : 0.25 * mm, "tangentPropagation" : true, "allowEdgeOverflow" : false});
        }
    });
